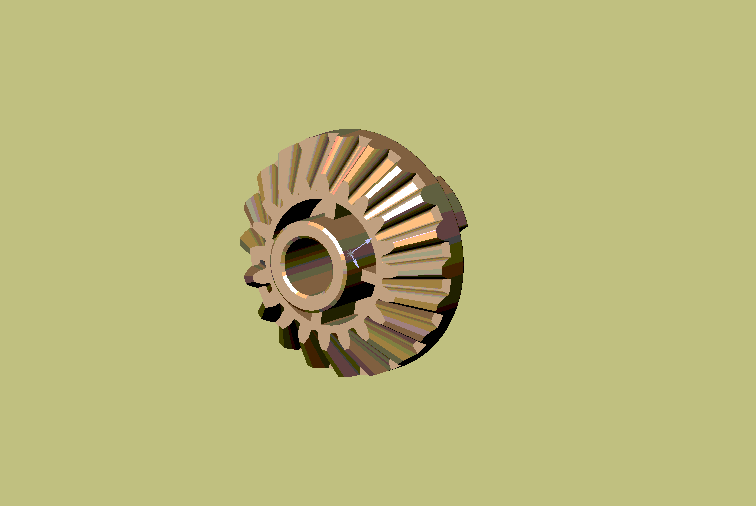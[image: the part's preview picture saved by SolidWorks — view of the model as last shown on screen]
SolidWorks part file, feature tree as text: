
SOLIDWORKS PART (.sldprt)
format: sldprt  version: not decoded by parser v0  size: 833,536 bytes
history: native  units: mm
features: sketch x25, plane x4, extrude x4, cut_extrude x3, fillet x2, pattern_circular x2, material x1, chamfer x1 + 1 further entry (+9 scaffold rows collapsed)
feature tree (52):
  scaffold x9  (default folders/planes/origin — collapsed)
  material  "Matériau <non spécifié>"
  plane  "Plane1"
  plane  "Plane2"
  plane  "Plane3"
  "Famille de pièces"
  sketch  "Esquisse1"  dims[c1.D2=11.0mm c1.D1=42.0mm c2.D1=9.0deg]
  sketch  "Esquisse2"  dims[c1.D2=~10.778873mm c1.D1=37.0mm c2.D1=~9.769674deg]
  sketch  "Esquisse3"  dims[c1.D2=~10.557746mm c1.D1=33.0mm c2.D1=~10.373081deg]
  sketch  "Esquisse4"  dims[c1.D2=~10.336619mm c1.D1=30.0mm c2.D1=~10.707917deg]
  sketch  "Esquisse5"  dims[c1.D2=~11.366667mm c1.D1=46.0mm c2.D1=7.4521deg]
  sketch  "Esquisse6"  dims[c1.D2=~11.733333mm c1.D1=50.0mm c2.D1=~5.640619deg]
  sketch  "Esquisse7"  dims[c1.D2=12.1mm c1.D1=54.0mm c2.D1=~3.619426deg]
  plane  "Plan1"  Offset=4mm
  sketch  "Esquisse8"  dims[c1.D2=7.0mm c1.D1=18.0mm c2.D1=9.0deg]
  sketch  "Esquisse9"  dims[c1.D2=~6.859283mm c1.D1=15.0mm c2.D1=~9.769674deg]
  sketch  "Esquisse10"  dims[c1.D2=~6.718566mm c1.D1=13.0mm c2.D1=~10.373081deg]
  sketch  "Esquisse11"  dims[c1.D2=~6.577848mm c1.D1=12.0mm c2.D1=~10.707917deg]
  sketch  "Esquisse12"  dims[c1.D2=~7.233333mm c1.D1=20.0mm c2.D1=7.4521deg]
  sketch  "Esquisse13"  dims[c1.D2=~7.466667mm c1.D1=21.0mm c2.D1=~5.640619deg]
  sketch  "Esquisse14"  dims[c1.D2=7.7mm c1.D1=22.0mm c2.D1=~3.619426deg]
  sketch  "Esquisse15"  dims[c1.D2=9.625mm c1.D1=23.0mm c2.D1=~10.707917deg]
  sketch  "Esquisse16"  dims[c1.D2=6.125mm c1.D1=10.0mm c2.D1=~10.707917deg]
  sketch  "Esquisse17"  dims[D1=19.25mm]
  sketch  "Esquisse18"  dims[D1=12.25mm]
  fillet  "Congé1"  Radius=0.25mm
  pattern_circular  "Répétition circulaire1"  Count=20 Angle=360deg
  sketch  "Esquisse19"  dims[D1=21.0mm]
  extrude  "Boss.-Extru.1"  Depth=2mm
  sketch  "Esquisse22"
  cut_extrude  "Enlèv. mat.-Extru.3"  [1 undecoded]
  sketch  "Esquisse24"  dims[D1=14.0mm]
  extrude  "Boss.-Extru.2"  Depth=3mm
  sketch  "Esquisse25"  dims[D2=14.0mm D3=8.0mm D1=5.0mm D4=1.5mm]
  extrude  "Boss.-Extru.3"  Depth=3mm
  fillet  "Congé2"  Radius=0.25mm
  sketch  "Esquisse27"  dims[D1=8.0mm]
  extrude  "Boss.-Extru.4"  Depth=2.5mm
  sketch  "Esquisse28"  dims[D1=5.0mm]
  cut_extrude  "Enlèv. mat.-Extru.5"  [1 undecoded]
  sketch  "Esquisse30"  dims[c1.D1=11.0mm c1.D2=~17.029386mm c2.D2=90.0deg c2.D4=~17.029386mm c2.D3=0.5mm]
  cut_extrude  "Enlèv. mat.-Extru.6"  Depth=5mm
  pattern_circular  "Répétition circulaire2"  Count=4 Angle=90deg
  chamfer  "Chanfrein1"  Distance=0.25mm Angle=45deg
decode coverage: 34 of 37 modeling features carry decoded parameters; 1 rows unclassified (native names shown)
note: ~ marks probable driven/reference dimensions
note: 2 parameter values undecoded
note: suppression state not decoded; provenance and decode notes live in map.json
